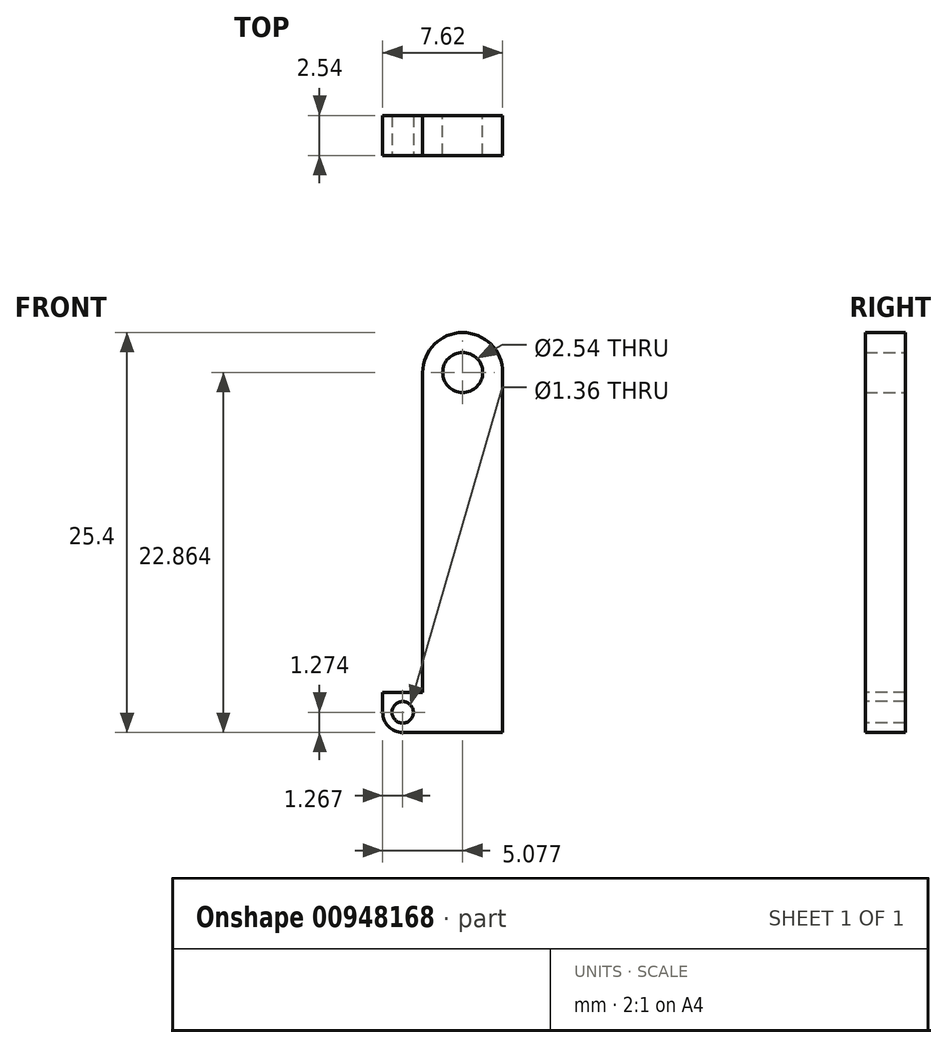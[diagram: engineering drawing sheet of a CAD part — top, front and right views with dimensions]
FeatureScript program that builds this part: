
annotation { "Feature Type Name" : "Feature", "Feature Type Description" : "" }
export const myFeature = defineFeature(function(context is Context, id is Id, definition is map)
    precondition{}
    {
        {
            var Q0;
            Q0=qCreatedBy(makeId("Front.planeOp"),FACE);
            var sketch = newSketch(context, id + "F0", { "sketchPlane" : qUnion([Q0])});
            skLineSegment(sketch, "E0.bottom", {"start": v(-37.87, 4.47) * mm, "end": v(-32.8, 4.47) * mm});
            skLineSegment(sketch, "E0.top", {"start": v(-37.87, -20.93) * mm, "end": v(-32.8, -20.93) * mm});
            skLineSegment(sketch, "E0.left", {"start": v(-37.87, 4.47) * mm, "end": v(-37.87, -20.93) * mm});
            skLineSegment(sketch, "E0.right", {"start": v(-32.8, 4.47) * mm, "end": v(-32.8, -20.93) * mm});
            skCircle(sketch, "E1", {"center": v(-35.33, 1.93) * mm, "radius": 1.27 * mm});
            skPoint(sketch, "E1.centerSnap0", {"position": v(-35.33, 4.47) * mm});
            skArc(sketch, "E2", {"start": v(-32.8, 1.93) * mm, "mid": v(-35.33, 4.47) * mm, "end": v(-37.87, 1.93) * mm});
            skSolve(sketch);
        }
        {
            var Q0;
            {var subQ1=sQuery(id+"F0.wireOp",EDGE,"E0.top");Q0=makeQuery(id+"F0.imprint","IMPRINT",FACE,{"disambiguationData":[TD([[makeQuery(id+"F0.imprint","IMPRINT",EDGE,{"derivedFrom":subQ1}),1.0]])]});}
            extrude(context, id + "F1", {"entities" : qUnion([Q0]), "depth" : 2.54 * mm, "offsetDistance" : 25.4 * mm});
        }
        {
            var Q0;
            Q0=makeQuery(id+"F1.opExtrude","SWEPT_FACE",FACE,{"disambiguationData":[OSD([sQuery(id+"F0.wireOp",EDGE,"E0.left")])]});
            var sketch = newSketch(context, id + "F2", { "sketchPlane" : qUnion([Q0])});
            skLineSegment(sketch, "E3.bottom", {"start": v(0, -15.85) * mm, "end": v(2.54, -15.85) * mm});
            skLineSegment(sketch, "E3.top", {"start": v(0, -20.93) * mm, "end": v(2.54, -20.93) * mm});
            skLineSegment(sketch, "E3.left", {"start": v(0, -15.85) * mm, "end": v(0, -20.93) * mm});
            skLineSegment(sketch, "E3.right", {"start": v(2.54, -15.85) * mm, "end": v(2.54, -20.93) * mm});
            skSolve(sketch);
        }
        {
            var Q0;
            Q0=makeQuery(id+"F2.imprint","IMPRINT",FACE,{"disambiguationData":[TD([[makeQuery(id+"F2.imprint","IMPRINT",EDGE,{"derivedFrom":sQuery(id+"F2.wireOp",EDGE,"E3.bottom")}),-1.0]])]});
            extrude(context, id + "F3", {"entities" : qUnion([Q0]), "operationType" : NewBodyOperationType.ADD, "depth" : 2.54 * mm, "offsetDistance" : 25.4 * mm});
        }
        {
            var Q0;
            Q0=makeQuery(id+"F3.boolean.opBoolean","MERGE",FACE,{"derivedFrom":[makeQuery(id+"F1.opExtrude","CAP_FACE",FACE,{"disambiguationData":[OSD([sQuery(id+"F0.wireOp",EDGE,"E0.top"),sQuery(id+"F0.wireOp",EDGE,"E0.left"),sQuery(id+"F0.wireOp",EDGE,"E0.right"),sQuery(id+"F0.wireOp",EDGE,"E1"),sQuery(id+"F0.wireOp",EDGE,"E2")])],"isStart":false}),makeQuery(id+"F3.opExtrude","SWEPT_FACE",FACE,{"disambiguationData":[OSD([sQuery(id+"F2.wireOp",EDGE,"E3.right")])]})]});
            var sketch = newSketch(context, id + "F4", { "sketchPlane" : qUnion([Q0])});
            skCircle(sketch, "E4", {"center": v(-39.14, -19.66) * mm, "radius": 0.68 * mm});
            skArc(sketch, "E5", {"start": v(-40.41, -19.66) * mm, "mid": v(-40.04, -20.55) * mm, "end": v(-39.14, -20.93) * mm});
            skLineSegment(sketch, "E6.bottom", {"start": v(-37.87, -15.85) * mm, "end": v(-40.41, -15.85) * mm});
            skLineSegment(sketch, "E6.top", {"start": v(-37.87, -18.39) * mm, "end": v(-40.41, -18.39) * mm});
            skLineSegment(sketch, "E6.left", {"start": v(-37.87, -15.85) * mm, "end": v(-37.87, -18.39) * mm});
            skLineSegment(sketch, "E6.right", {"start": v(-40.41, -15.85) * mm, "end": v(-40.41, -18.39) * mm});
            skSolve(sketch);
        }
        {
            var Q0;
            Q0=makeQuery(id+"F4.imprint","IMPRINT",FACE,{"disambiguationData":[TD([[makeQuery(id+"F4.imprint","IMPRINT",EDGE,{"derivedFrom":sQuery(id+"F4.wireOp",EDGE,"E6.bottom")}),-1.0]])]});
            var Q1;
            Q1=makeQuery(id+"F4.imprint","IMPRINT",FACE,{"disambiguationData":[TD([[makeQuery(id+"F4.imprint","IMPRINT",EDGE,{"derivedFrom":sQuery(id+"F4.wireOp",EDGE,"E4")}),1.0]])]});
            var Q2;
            {var subQ0=sQuery(id+"F4.wireOp",EDGE,"E5");Q2=makeQuery(id+"F4.imprint","IMPRINT",FACE,{"disambiguationData":[TD([[makeQuery(id+"F4.imprint","IMPRINT",EDGE,{"derivedFrom":subQ0}),-1.0]])]});}
            extrude(context, id + "F5", {"entities" : qUnion([Q0, Q1, Q2]), "operationType" : NewBodyOperationType.REMOVE, "oppositeDirection" : true, "depth" : 25.4 * mm, "offsetDistance" : 25.4 * mm});
        }
    });
